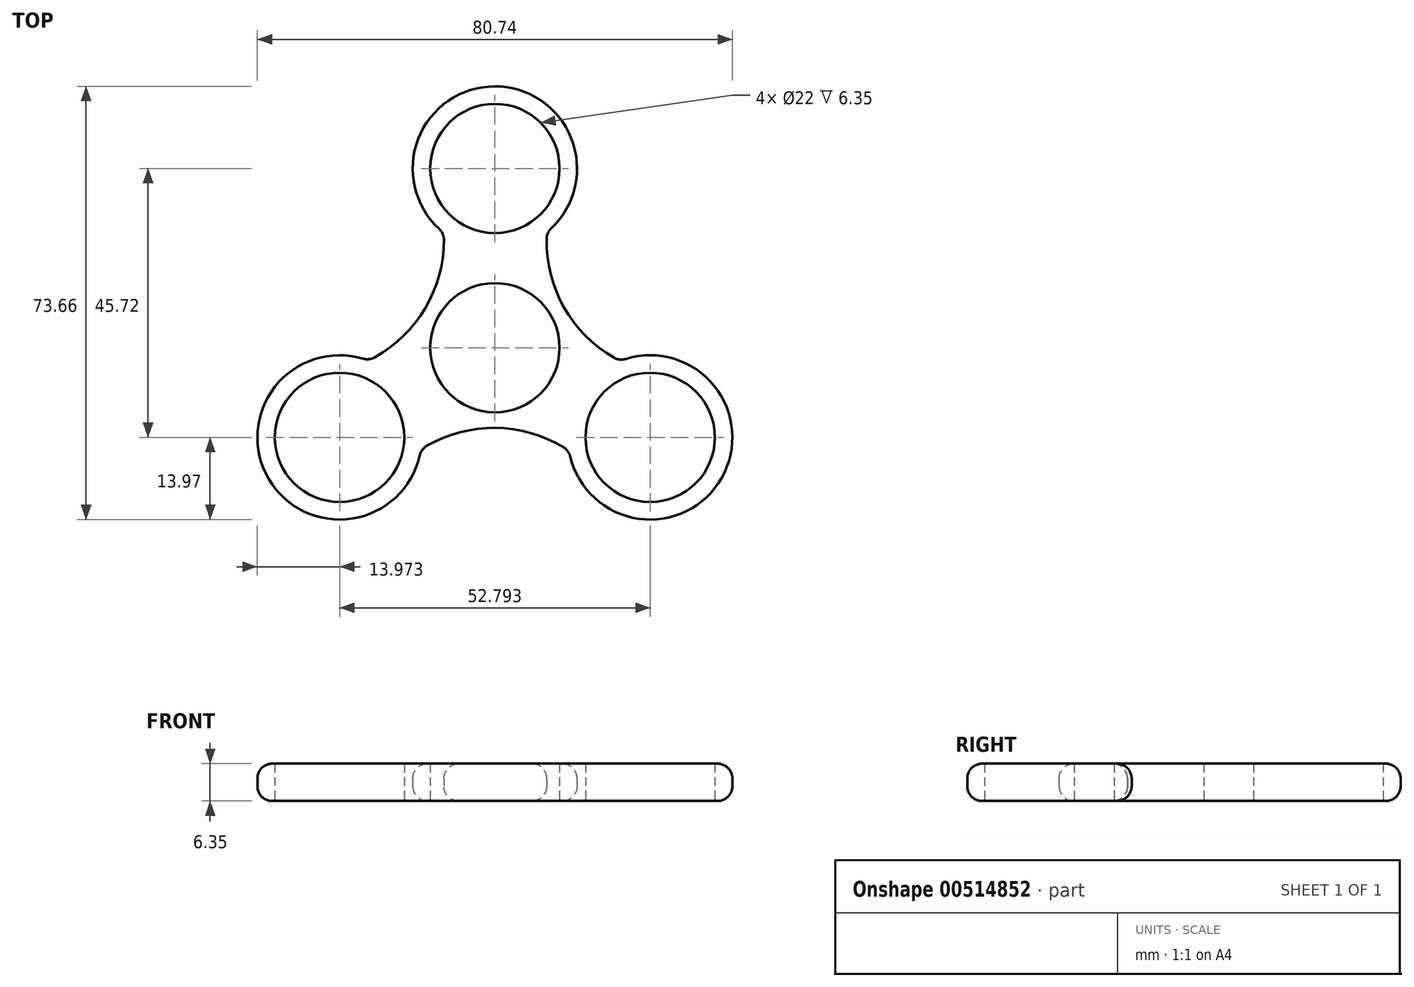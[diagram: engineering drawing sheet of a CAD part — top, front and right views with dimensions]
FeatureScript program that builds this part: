
annotation { "Feature Type Name" : "Feature", "Feature Type Description" : "" }
export const myFeature = defineFeature(function(context is Context, id is Id, definition is map)
    precondition{}
    {
        {
            var Q0;
            Q0=qCreatedBy(makeId("Top.planeOp"),FACE);
            var sketch = newSketch(context, id + "F0", { "sketchPlane" : qUnion([Q0])});
            skCircle(sketch, "E0", {"center": v(0, 0) * mm, "radius": 44.45 * mm});
            skCircle(sketch, "E1", {"center": v(0, 0) * mm, "radius": 11 * mm});
            skLineSegment(sketch, "E2", {"start": v(0, 0) * mm, "end": v(0, 30.48) * mm});
            skCircle(sketch, "E3", {"center": v(0, 30.48) * mm, "radius": 11 * mm});
            skCircle(sketch, "E4", {"center": v(0, 30.48) * mm, "radius": 13.97 * mm});
            skCircle(sketch, "E5.1.0", {"center": v(-26.4, -15.24) * mm, "radius": 13.97 * mm});
            skCircle(sketch, "E5.1.1", {"center": v(-26.4, -15.24) * mm, "radius": 11 * mm});
            skCircle(sketch, "E5.2.0", {"center": v(26.4, -15.24) * mm, "radius": 13.97 * mm});
            skCircle(sketch, "E5.2.1", {"center": v(26.4, -15.24) * mm, "radius": 11 * mm});
            skCircle(sketch, "E6", {"center": v(0, 0) * mm, "radius": 13.97 * mm});
            skArc(sketch, "E7", {"start": v(12.61, -17.51) * mm, "mid": v(0.05, -13.62) * mm, "end": v(-12.58, -17.3) * mm});
            skArc(sketch, "E8.1.0", {"start": v(8.86, 19.68) * mm, "mid": v(11.77, 6.85) * mm, "end": v(21.27, -2.25) * mm});
            skArc(sketch, "E8.2.0", {"start": v(-21.47, -2.17) * mm, "mid": v(-11.82, 6.76) * mm, "end": v(-8.69, 19.54) * mm});
            skSolve(sketch);
        }
        {
            var Q0;
            Q0=makeQuery(id+"F0.imprint","IMPRINT",FACE,{"disambiguationData":[TD([[makeQuery(id+"F0.imprint","IMPRINT",EDGE,{"derivedFrom":sQuery(id+"F0.wireOp",EDGE,"E3")}),-1.0]])]});
            var Q1;
            Q1=makeQuery(id+"F0.imprint","IMPRINT",FACE,{"disambiguationData":[TD([[makeQuery(id+"F0.imprint","IMPRINT",EDGE,{"derivedFrom":sQuery(id+"F0.wireOp",EDGE,"E5.2.0")}),1.0]])]});
            var Q2;
            Q2=makeQuery(id+"F0.imprint","IMPRINT",FACE,{"disambiguationData":[TD([[makeQuery(id+"F0.imprint","IMPRINT",EDGE,{"derivedFrom":sQuery(id+"F0.wireOp",EDGE,"E5.1.0")}),1.0]])]});
            var Q3;
            Q3=makeQuery(id+"F0.imprint","IMPRINT",FACE,{"disambiguationData":[TD([[makeQuery(id+"F0.imprint","IMPRINT",EDGE,{"derivedFrom":sQuery(id+"F0.wireOp",EDGE,"E1")}),-1.0]])]});
            var Q4;
            {var subQ0=sQuery(id+"F0.wireOp",EDGE,"E4");var subQ1=sQuery(id+"F0.wireOp",EDGE,"E2");var subQ2=makeQuery(id+"F0.imprint","INTERSECT",VERTEX,{"derivedFrom":[subQ1,subQ0]});Q4=makeQuery(id+"F0.imprint","IMPRINT",FACE,{"disambiguationData":[TD([[makeQuery(id+"F0.imprint","IMPRINT",EDGE,{"disambiguationData":[TD([[subQ2,1.0]])],"derivedFrom":subQ1}),1.0]])]});}
            var Q5;
            {var subQ0=sQuery(id+"F0.wireOp",EDGE,"E4");var subQ1=sQuery(id+"F0.wireOp",EDGE,"E2");var subQ2=makeQuery(id+"F0.imprint","INTERSECT",VERTEX,{"derivedFrom":[subQ1,subQ0]});Q5=makeQuery(id+"F0.imprint","IMPRINT",FACE,{"disambiguationData":[TD([[makeQuery(id+"F0.imprint","IMPRINT",EDGE,{"disambiguationData":[TD([[subQ2,1.0]])],"derivedFrom":subQ1}),-1.0]])]});}
            var Q6;
            {var subQ0=sQuery(id+"F0.wireOp",EDGE,"E7");var subQ1=sQuery(id+"F0.wireOp",EDGE,"E5.2.0");var subQ2=makeQuery(id+"F0.imprint","INTERSECT",VERTEX,{"derivedFrom":[subQ1,subQ0]});Q6=makeQuery(id+"F0.imprint","IMPRINT",FACE,{"disambiguationData":[TD([[makeQuery(id+"F0.imprint","IMPRINT",EDGE,{"disambiguationData":[TD([[subQ2,1.0]])],"derivedFrom":subQ1}),-1.0]])]});}
            var Q7;
            {var subQ0=sQuery(id+"F0.wireOp",EDGE,"E7");var subQ1=sQuery(id+"F0.wireOp",EDGE,"E5.1.0");var subQ2=makeQuery(id+"F0.imprint","INTERSECT",VERTEX,{"derivedFrom":[subQ1,subQ0]});Q7=makeQuery(id+"F0.imprint","IMPRINT",FACE,{"disambiguationData":[TD([[makeQuery(id+"F0.imprint","IMPRINT",EDGE,{"disambiguationData":[TD([[subQ2,-1.0]])],"derivedFrom":subQ1}),-1.0]])]});}
            extrude(context, id + "F1", {"entities" : qUnion([Q0, Q1, Q2, Q3, Q4, Q5, Q6, Q7]), "depth" : 6.35 * mm, "offsetDistance" : 25.4 * mm});
        }
        {
            var Q0;
            Q0=makeQuery(id+"F1.opExtrude","CAP_EDGE",EDGE,{"disambiguationData":[OSD([sQuery(id+"F0.wireOp",EDGE,"E8.1.0")])],"isStart":false});
            var Q1;
            Q1=makeQuery(id+"F1.opExtrude","CAP_EDGE",EDGE,{"disambiguationData":[OSD([sQuery(id+"F0.wireOp",EDGE,"E8.2.0")])],"isStart":false});
            var Q2;
            Q2=makeQuery(id+"F1.opExtrude","CAP_EDGE",EDGE,{"disambiguationData":[OSD([sQuery(id+"F0.wireOp",EDGE,"E7")])],"isStart":false});
            var Q3;
            Q3=makeQuery(id+"F1.opExtrude","CAP_EDGE",EDGE,{"disambiguationData":[OSD([sQuery(id+"F0.wireOp",EDGE,"E8.2.0")])],"isStart":true});
            var Q4;
            Q4=makeQuery(id+"F1.opExtrude","CAP_EDGE",EDGE,{"disambiguationData":[OSD([sQuery(id+"F0.wireOp",EDGE,"E8.1.0")])],"isStart":true});
            var Q5;
            Q5=makeQuery(id+"F1.opExtrude","CAP_EDGE",EDGE,{"disambiguationData":[OSD([sQuery(id+"F0.wireOp",EDGE,"E7")])],"isStart":true});
            var Q6;
            Q6=makeQuery(id+"F1.opExtrude","SWEPT_FACE",FACE,{"disambiguationData":[OSD([sQuery(id+"F0.wireOp",EDGE,"E4")])]});
            var Q7;
            Q7=makeQuery(id+"F1.opExtrude","SWEPT_FACE",FACE,{"disambiguationData":[OSD([sQuery(id+"F0.wireOp",EDGE,"E5.2.0")])]});
            var Q8;
            Q8=makeQuery(id+"F1.opExtrude","SWEPT_FACE",FACE,{"disambiguationData":[OSD([sQuery(id+"F0.wireOp",EDGE,"E5.1.0")])]});
            fillet(context, id + "F2", {"entities" : qUnion([Q0, Q1, Q2, Q3, Q4, Q5, Q6, Q7, Q8]), "radius" : 2.54 * mm, "tangentPropagation" : true, "allowEdgeOverflow" : false});
        }
    });
